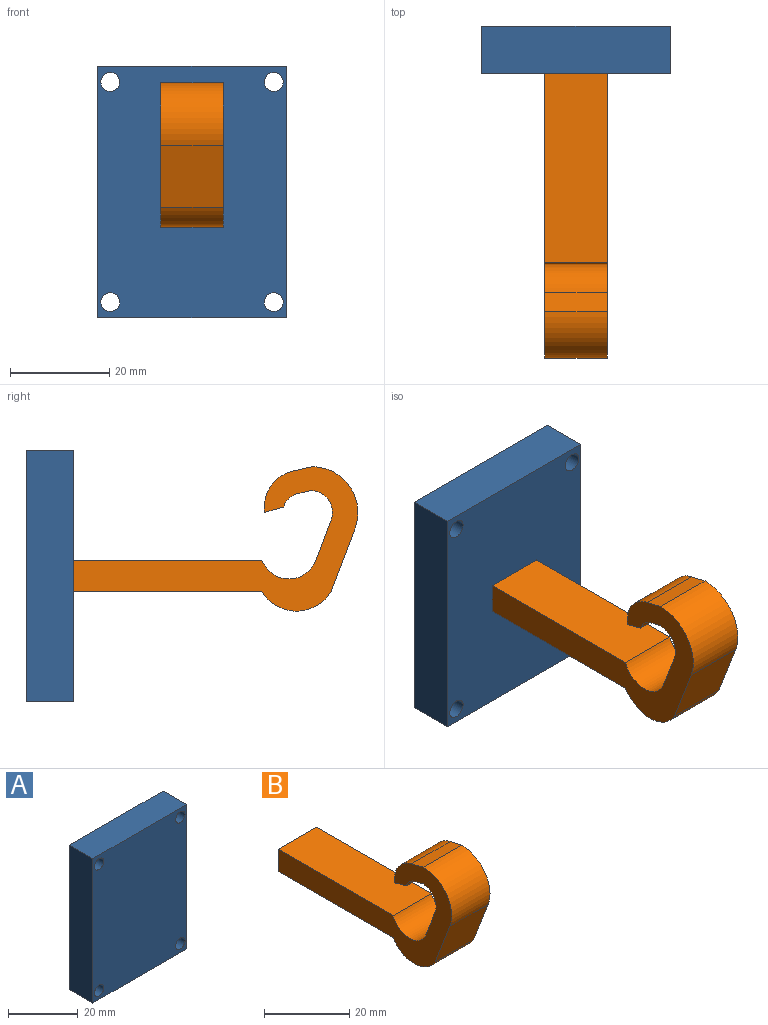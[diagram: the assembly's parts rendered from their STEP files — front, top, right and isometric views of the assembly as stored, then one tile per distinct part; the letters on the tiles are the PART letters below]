
ASSEMBLY  parts=2 mates=1
PART A: 10 faces, bbox 38.1x9.5x50.8 mm
  f0: plane 50.8x9.53mm, normal (-1,0,0), area 483.9mm2, adj f1,f7,f8,f9
  f1: plane 38.1x9.53mm, normal (0,0,-1), area 362.9mm2, adj f0,f2,f8,f9
  f2: plane 50.8x9.53mm, normal (1,0,0), area 483.9mm2, adj f1,f7,f8,f9
  f3: cylinder r=1.91mm len=9.53mm, axis (0,1,0), area 114mm2, adj f8,f9
  f4: cylinder r=1.91mm len=9.53mm, axis (0,1,0), area 114mm2, adj f8,f9
  f5: cylinder r=1.91mm len=9.53mm, axis (0,1,0), area 114mm2, adj f8,f9
  f6: cylinder r=1.91mm len=9.53mm, axis (0,1,0), area 114mm2, adj f8,f9
  f7: plane 38.1x9.53mm, normal (0,0,1), area 362.9mm2, adj f0,f2,f8,f9
  f8: plane 50.8x38.1mm, normal (0,-1,0), area 1889.9mm2, adj f0,f1,f2,f3,f4,f5,f6,f7
  f9: plane 50.8x38.1mm, normal (0,1,0), area 1889.9mm2, adj f0,f1,f2,f3,f4,f5,f6,f7
PART B: 17 faces, bbox 12.7x57.5x29.2 mm
  f0: plane 38.1x12.7mm, normal (0,0,1), area 483.9mm2, adj f1,f14,f15,f16
  f1: cylinder r=5.82mm len=12.7mm, axis (-1,0,0), area 179.1mm2, adj f0,f2,f15,f16
  f2: plane 12.7x8.13mm, normal (0,0.94,0.35), area 110.3mm2, adj f1,f3,f15,f16
  f3: cylinder r=4.42mm len=12.7mm, axis (-1,0,0), area 105.7mm2, adj f2,f4,f15,f16
  f4: plane 12.7x2.78mm, normal (0,-0.23,-0.97), area 36.2mm2, adj f3,f5,f15,f16
  f5: cylinder r=3.92mm len=12.7mm, axis (-1,0,0), area 52.3mm2, adj f4,f6,f15,f16
  f6: plane 12.7x3.83mm, normal (0,-0.27,-0.96), area 50.4mm2, adj f5,f7,f15,f16
  f7: cylinder r=7.4mm len=12.7mm, axis (-1,0,0), area 140mm2, adj f6,f8,f15,f16
  f8: plane 12.7x3.84mm, normal (0,0.23,0.97), area 50.1mm2, adj f7,f9,f15,f16
  f9: cylinder r=9.26mm len=12.7mm, axis (-1,0,0), area 229.1mm2, adj f8,f10,f15,f16
  f10: plane 12.7x12.58mm, normal (0,-0.93,-0.36), area 171.2mm2, adj f9,f11,f15,f16
  f11: cylinder r=8.1mm len=13.96mm, axis (-1,0,0), area 213.7mm2, adj f10,f12,f15,f16
  f12: plane 12.7x0.07mm, normal (0,-1,0), area 0.9mm2, adj f11,f13,f15,f16
  f13: plane 38.1x12.7mm, normal (0,0,-1), area 483.9mm2, adj f12,f14,f15,f16
  f14: plane 12.7x6.35mm, normal (0,1,0), area 80.6mm2, adj f0,f13,f15,f16
  f15: plane 57.5x29.15mm, normal (1,0,0), area 501.4mm2, adj f0,f1,f2,f3,f4,f5,f6,f7
  f16: plane 57.5x29.15mm, normal (-1,0,0), area 501.4mm2, adj f0,f1,f2,f3,f4,f5,f6,f7
PLACE A t=(0.82,-0.8,-8.03)mm
PLACE B t=(0.82,-24.61,-8.03)mm
MATE fastened B.f14 <-> A.f8  axis (0,1,0) through (0.82,-5.56,-8.03)mm
